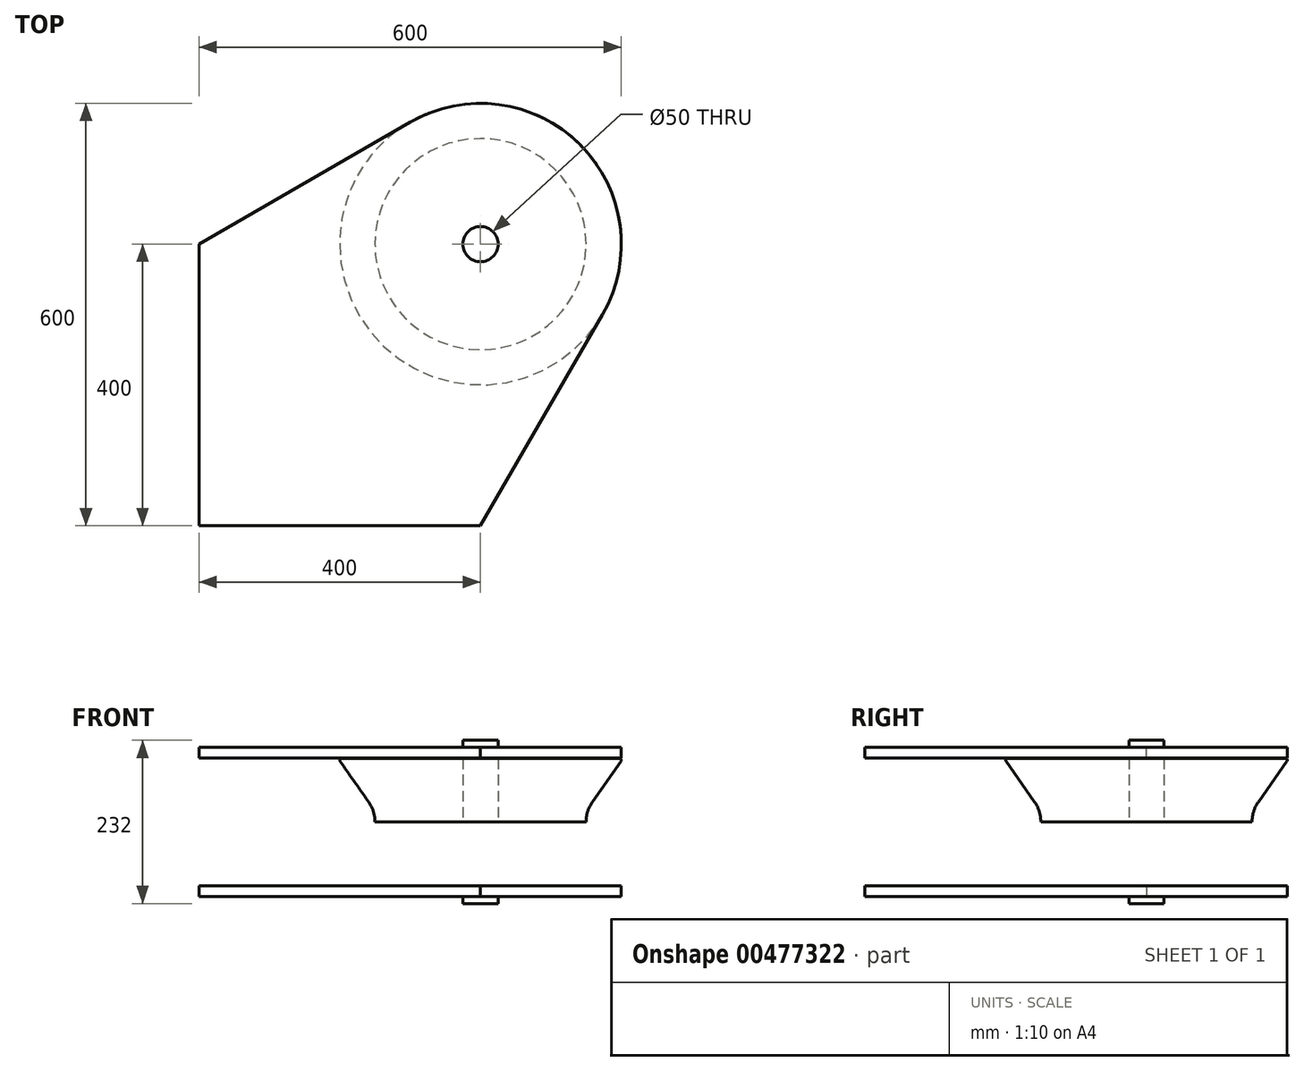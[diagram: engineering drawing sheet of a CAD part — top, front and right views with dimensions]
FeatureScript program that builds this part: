
annotation { "Feature Type Name" : "Feature", "Feature Type Description" : "" }
export const myFeature = defineFeature(function(context is Context, id is Id, definition is map)
    precondition{}
    {
        {
            var Q0;
            Q0=qCreatedBy(makeId("Right.planeOp"),FACE);
            var sketch = newSketch(context, id + "F0", { "sketchPlane" : qUnion([Q0])});
            skArc(sketch, "E0", {"start": v(159.15, 28.83) * mm, "mid": v(152.34, 15.13) * mm, "end": v(150, 0) * mm});
            skArc(sketch, "E1", {"start": v(199.54, 86.06) * mm, "mid": v(199.72, 88.65) * mm, "end": v(197.5, 90) * mm});
            skLineSegment(sketch, "E2", {"start": v(150, 0) * mm, "end": v(0, 0) * mm});
            skLineSegment(sketch, "E3", {"start": v(200, 106) * mm, "end": v(0, 106) * mm});
            skLineSegment(sketch, "E4", {"start": v(0, 106) * mm, "end": v(0, 91) * mm});
            skLineSegment(sketch, "E5", {"start": v(0, 91) * mm, "end": v(200, 91) * mm});
            skLineSegment(sketch, "E6", {"start": v(200, 91) * mm, "end": v(200, 106) * mm});
            skLineSegment(sketch, "E7", {"start": v(197.5, 90) * mm, "end": v(25, 90) * mm});
            skLineSegment(sketch, "E8", {"start": v(199.54, 86.06) * mm, "end": v(159.15, 28.83) * mm});
            skLineSegment(sketch, "E9", {"start": v(0, 116) * mm, "end": v(25, 116) * mm});
            skLineSegment(sketch, "E10", {"start": v(25, 116) * mm, "end": v(25, 0) * mm});
            skLineSegment(sketch, "E11", {"start": v(25, 0) * mm, "end": v(0, 0) * mm});
            skLineSegment(sketch, "E12", {"start": v(0, 0) * mm, "end": v(0, 116) * mm});
            skSolve(sketch);
        }
        {
            var Q0;
            {var subQ5=sQuery(id+"F0.wireOp",EDGE,"E9");Q0=makeQuery(id+"F0.imprint","IMPRINT",FACE,{"disambiguationData":[TD([[makeQuery(id+"F0.imprint","IMPRINT",EDGE,{"derivedFrom":subQ5}),-1.0]])]});}
            var Q1;
            {var subQ0=sQuery(id+"F0.wireOp",EDGE,"E12");var subQ1=sQuery(id+"F0.wireOp",EDGE,"E3");var subQ2=makeQuery(id+"F0.imprint","INTERSECT",VERTEX,{"derivedFrom":[subQ1,subQ0]});Q1=makeQuery(id+"F0.imprint","IMPRINT",FACE,{"disambiguationData":[TD([[makeQuery(id+"F0.imprint","IMPRINT",EDGE,{"disambiguationData":[TD([[subQ2,1.0]])],"derivedFrom":subQ1}),1.0]])]});}
            var Q2;
            {var subQ0=sQuery(id+"F0.wireOp",EDGE,"E11");Q2=makeQuery(id+"F0.imprint","IMPRINT",FACE,{"disambiguationData":[TD([[makeQuery(id+"F0.imprint","IMPRINT",EDGE,{"derivedFrom":subQ0}),-1.0]])]});}
            var Q3;
            Q3=sQuery(id+"F0.wireOp",EDGE,"E12");
            revolve(context, id + "F1", {"entities" : qUnion([Q0, Q1, Q2]), "axis" : qUnion([Q3]), "revolveType" : RevolveType.FULL});
        }
        {
            var Q0;
            Q0=makeQuery(id+"F0.imprint","IMPRINT",FACE,{"disambiguationData":[TD([[makeQuery(id+"F0.imprint","IMPRINT",EDGE,{"derivedFrom":sQuery(id+"F0.wireOp",EDGE,"E0")}),-1.0]])]});
            var Q1;
            Q1=sQuery(id+"F0.wireOp",EDGE,"E12");
            revolve(context, id + "F2", {"operationType" : NewBodyOperationType.ADD, "entities" : qUnion([Q0]), "axis" : qUnion([Q1]), "revolveType" : RevolveType.FULL});
        }
        {
            var Q0;
            {var subQ0=sQuery(id+"F0.wireOp",EDGE,"E6");Q0=makeQuery(id+"F0.imprint","IMPRINT",FACE,{"disambiguationData":[TD([[makeQuery(id+"F0.imprint","IMPRINT",EDGE,{"derivedFrom":subQ0}),1.0]])]});}
            var Q1;
            Q1=sQuery(id+"F0.wireOp",EDGE,"E12");
            revolve(context, id + "F3", {"operationType" : NewBodyOperationType.ADD, "entities" : qUnion([Q0]), "axis" : qUnion([Q1]), "revolveType" : RevolveType.FULL});
        }
        {
            var Q0;
            Q0=makeQuery(id+"F3.opRevolve","SWEPT_FACE",FACE,{"disambiguationData":[OSD([sQuery(id+"F0.wireOp",EDGE,"E3")])]});
            var sketch = newSketch(context, id + "F4", { "sketchPlane" : qUnion([Q0])});
            skLineSegment(sketch, "E13.bottom", {"start": v(0, 0) * mm, "end": v(-400, 0) * mm});
            skLineSegment(sketch, "E13.top", {"start": v(0, -400) * mm, "end": v(-400, -400) * mm});
            skLineSegment(sketch, "E13.left", {"start": v(0, 0) * mm, "end": v(0, -400) * mm});
            skLineSegment(sketch, "E13.right", {"start": v(-400, 0) * mm, "end": v(-400, -400) * mm});
            skLineSegment(sketch, "E14", {"start": v(-400, 0) * mm, "end": v(-100, 173.2) * mm});
            skLineSegment(sketch, "E15", {"start": v(0, -400) * mm, "end": v(173.2, -100) * mm});
            skSolve(sketch);
        }
        {
            var Q0;
            {var subQ1=sQuery(id+"F4.wireOp",EDGE,"E13.top");Q0=makeQuery(id+"F4.imprint","IMPRINT",FACE,{"disambiguationData":[TD([[makeQuery(id+"F4.imprint","IMPRINT",EDGE,{"derivedFrom":subQ1}),-1.0]])]});}
            var Q1;
            {var subQ0=sQuery(id+"F4.wireOp",EDGE,"E14");Q1=makeQuery(id+"F4.imprint","IMPRINT",FACE,{"disambiguationData":[TD([[makeQuery(id+"F4.imprint","IMPRINT",EDGE,{"derivedFrom":subQ0}),-1.0]])]});}
            var Q2;
            {var subQ0=sQuery(id+"F4.wireOp",EDGE,"E15");Q2=makeQuery(id+"F4.imprint","IMPRINT",FACE,{"disambiguationData":[TD([[makeQuery(id+"F4.imprint","IMPRINT",EDGE,{"derivedFrom":subQ0}),1.0]])]});}
            var Q3;
            Q3=makeQuery(id+"F3.opRevolve","SWEPT_FACE",FACE,{"disambiguationData":[OSD([sQuery(id+"F0.wireOp",EDGE,"E5")])]});
            extrude(context, id + "F5", {"entities" : qUnion([Q0, Q1, Q2]), "operationType" : NewBodyOperationType.ADD, "endBound" : BoundingType.UP_TO_SURFACE, "oppositeDirection" : true, "endBoundEntityFace" : qUnion([Q3]), "depth" : 25 * mm});
        }
        {
            var Q0;
            Q0=makeQuery(id+"F1.opRevolve","SWEPT_BODY",BODY,{"disambiguationData":[OSD([sQuery(id+"F0.wireOp",EDGE,"E9"),sQuery(id+"F0.wireOp",EDGE,"E10"),sQuery(id+"F0.wireOp",EDGE,"E11"),sQuery(id+"F0.wireOp",EDGE,"E12")])]});
            var Q1;
            Q1=makeQuery(id+"F2.boolean.opBoolean","MERGE",FACE,{"derivedFrom":[makeQuery(id+"F1.opRevolve","SWEPT_FACE",FACE,{"disambiguationData":[OSD([sQuery(id+"F0.wireOp",EDGE,"E11")])]}),makeQuery(id+"F2.opRevolve","SWEPT_FACE",FACE,{"disambiguationData":[OSD([sQuery(id+"F0.wireOp",EDGE,"E2")])]})]});
            mirror(context, id + "F6", {"operationType" : NewBodyOperationType.ADD, "entities" : qUnion([Q0]), "mirrorPlane" : qUnion([Q1])});
        }
    });
